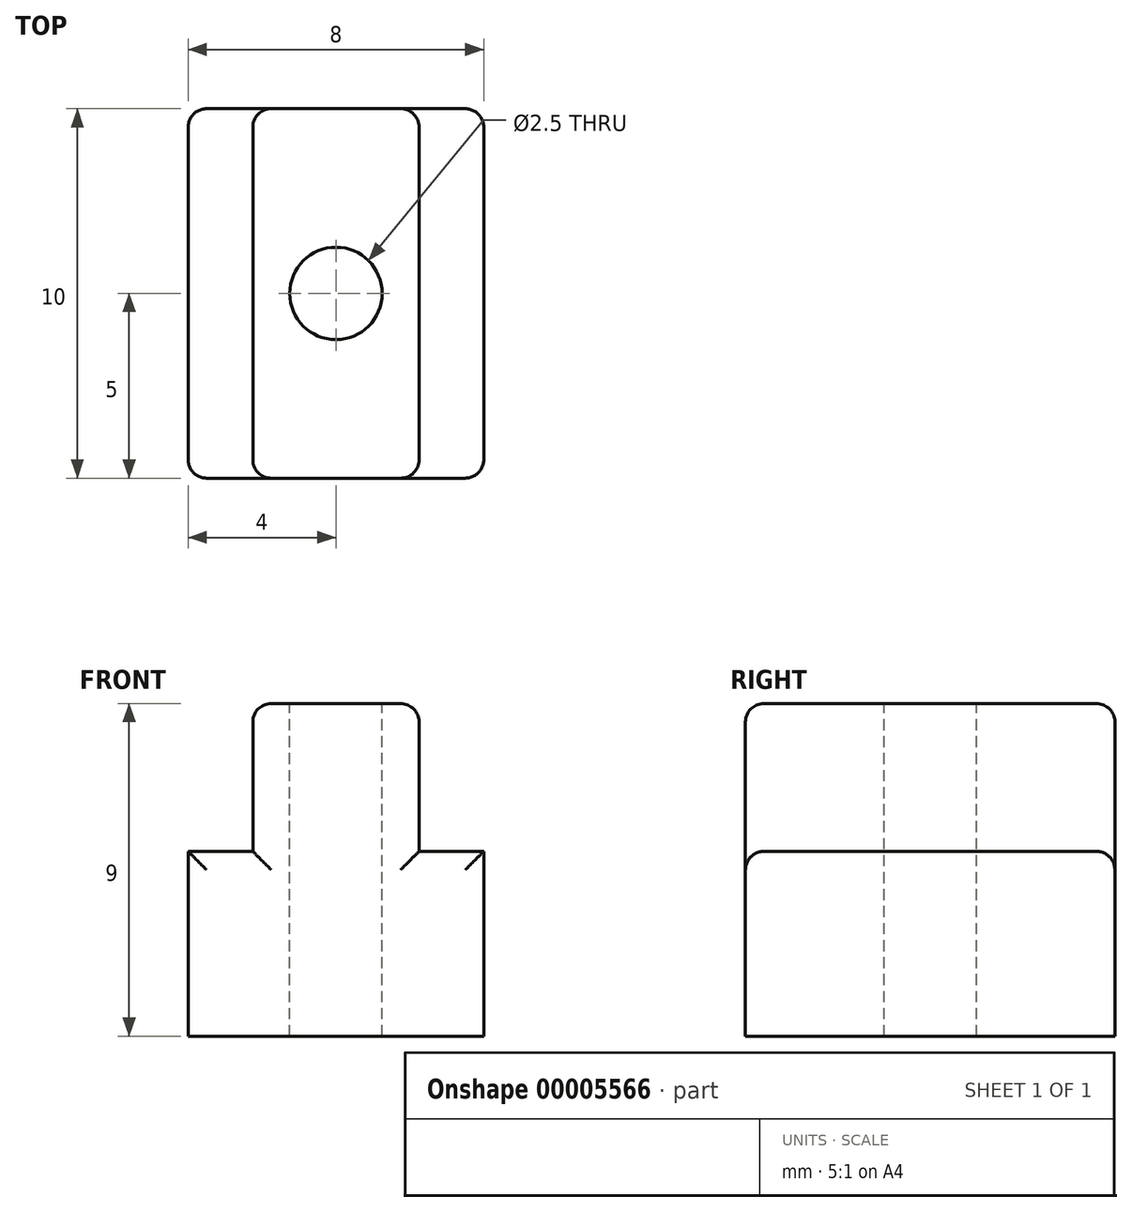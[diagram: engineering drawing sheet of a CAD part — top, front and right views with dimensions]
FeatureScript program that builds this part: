
annotation { "Feature Type Name" : "Feature", "Feature Type Description" : "" }
export const myFeature = defineFeature(function(context is Context, id is Id, definition is map)
    precondition{}
    {
        {
            var Q0;
            Q0=qCreatedBy(makeId("Front.planeOp"),FACE);
            var sketch = newSketch(context, id + "F0", { "sketchPlane" : qUnion([Q0])});
            skLineSegment(sketch, "E0.bottom", {"start": v(4, -5) * mm, "end": v(-4, -5) * mm});
            skLineSegment(sketch, "E0.top", {"start": v(4, 0) * mm, "end": v(-4, 0) * mm});
            skLineSegment(sketch, "E0.left", {"start": v(4, -5) * mm, "end": v(4, 0) * mm});
            skLineSegment(sketch, "E0.right", {"start": v(-4, -5) * mm, "end": v(-4, 0) * mm});
            skLineSegment(sketch, "E1.bottom", {"start": v(-2.25, 4) * mm, "end": v(2.25, 4) * mm});
            skLineSegment(sketch, "E1.top", {"start": v(-2.25, 0) * mm, "end": v(2.25, 0) * mm});
            skLineSegment(sketch, "E1.left", {"start": v(-2.25, 4) * mm, "end": v(-2.25, 0) * mm});
            skLineSegment(sketch, "E1.right", {"start": v(2.25, 4) * mm, "end": v(2.25, 0) * mm});
            skSolve(sketch);
        }
        {
            var Q0;
            {Q0=qUnion([makeQuery(id+"F0.imprint","IMPRINT",FACE,{"disambiguationData":[TD([[makeQuery(id+"F0.imprint","IMPRINT",EDGE,{"derivedFrom":sQuery(id+"F0.wireOp",EDGE,"E0.bottom")}),-1.0]])]}),makeQuery(id+"F0.imprint","IMPRINT",FACE,{"disambiguationData":[TD([[makeQuery(id+"F0.imprint","IMPRINT",EDGE,{"derivedFrom":sQuery(id+"F0.wireOp",EDGE,"E1.bottom")}),-1.0]])]})]);}
            extrude(context, id + "F1", {"entities" : qUnion([Q0]), "depth" : 10 * mm});
        }
        {
            var Q0;
            Q0=makeQuery(id+"F1.opExtrude","SWEPT_FACE",FACE,{"disambiguationData":[OSD([sQuery(id+"F0.wireOp",EDGE,"E1.bottom")])]});
            var sketch = newSketch(context, id + "F2", { "sketchPlane" : qUnion([Q0])});
            skLineSegment(sketch, "E2", {"start": v(0, -10) * mm, "end": v(0, 0) * mm, "construction": true});
            skCircle(sketch, "E3", {"center": v(0, -5) * mm, "radius": 1.25 * mm});
            skSolve(sketch);
        }
        {
            var Q0;
            Q0=makeQuery(id+"F2.imprint","IMPRINT",FACE,{"disambiguationData":[TD([[makeQuery(id+"F2.imprint","IMPRINT",EDGE,{"derivedFrom":sQuery(id+"F2.wireOp",EDGE,"E3")}),1.0]])]});
            var Q1;
            Q1=makeQuery(id+"F1.opExtrude","SWEPT_FACE",FACE,{"disambiguationData":[OSD([sQuery(id+"F0.wireOp",EDGE,"E0.bottom")])]});
            extrude(context, id + "F3", {"entities" : qUnion([Q0]), "operationType" : NewBodyOperationType.REMOVE, "endBound" : BoundingType.UP_TO_SURFACE, "oppositeDirection" : true, "endBoundEntityFace" : qUnion([Q1]), "depth" : 25 * mm});
        }
        {
            var Q0;
            Q0=makeQuery(id+"F1.opExtrude","SWEPT_EDGE",EDGE,{"disambiguationData":[OSD([sQuery(id+"F0.wireOp",EDGE,"E1.bottom"),sQuery(id+"F0.wireOp",EDGE,"E1.right")])]});
            var Q1;
            Q1=makeQuery(id+"F1.opExtrude","CAP_EDGE",EDGE,{"disambiguationData":[OSD([sQuery(id+"F0.wireOp",EDGE,"E1.bottom")])],"isStart":false});
            var Q2;
            Q2=makeQuery(id+"F1.opExtrude","SWEPT_EDGE",EDGE,{"disambiguationData":[OSD([sQuery(id+"F0.wireOp",EDGE,"E1.bottom"),sQuery(id+"F0.wireOp",EDGE,"E1.left")])]});
            var Q3;
            Q3=makeQuery(id+"F1.opExtrude","CAP_EDGE",EDGE,{"disambiguationData":[OSD([sQuery(id+"F0.wireOp",EDGE,"E1.bottom")])],"isStart":true});
            var Q4;
            Q4=makeQuery(id+"F1.opExtrude","CAP_EDGE",EDGE,{"disambiguationData":[OSD([sQuery(id+"F0.wireOp",EDGE,"E1.left")])],"isStart":true});
            var Q5;
            {var subQ0=sQuery(id+"F0.wireOp",EDGE,"E0.top");Q5=makeQuery(id+"F1.opExtrude","CAP_EDGE",EDGE,{"disambiguationData":[OSD([subQ0]),TDD([makeQuery(id+"F0.imprint","IMPRINT",EDGE,{"disambiguationData":[TD([[makeQuery(id+"F0.imprint","INTERSECT",VERTEX,{"derivedFrom":[subQ0,sQuery(id+"F0.wireOp",EDGE,"E0.right")]}),1.0]])],"derivedFrom":subQ0})])],"isStart":true});}
            var Q6;
            Q6=makeQuery(id+"F1.opExtrude","CAP_EDGE",EDGE,{"disambiguationData":[OSD([sQuery(id+"F0.wireOp",EDGE,"E0.right")])],"isStart":true});
            var Q7;
            {var subQ0=sQuery(id+"F0.wireOp",EDGE,"E0.top");Q7=makeQuery(id+"F1.opExtrude","CAP_EDGE",EDGE,{"disambiguationData":[OSD([subQ0]),TDD([makeQuery(id+"F0.imprint","IMPRINT",EDGE,{"disambiguationData":[TD([[makeQuery(id+"F0.imprint","INTERSECT",VERTEX,{"derivedFrom":[subQ0,sQuery(id+"F0.wireOp",EDGE,"E0.right")]}),1.0]])],"derivedFrom":subQ0})])],"isStart":false});}
            var Q8;
            Q8=makeQuery(id+"F1.opExtrude","CAP_EDGE",EDGE,{"disambiguationData":[OSD([sQuery(id+"F0.wireOp",EDGE,"E1.left")])],"isStart":false});
            var Q9;
            Q9=makeQuery(id+"F1.opExtrude","CAP_EDGE",EDGE,{"disambiguationData":[OSD([sQuery(id+"F0.wireOp",EDGE,"E0.right")])],"isStart":false});
            var Q10;
            Q10=makeQuery(id+"F1.opExtrude","CAP_EDGE",EDGE,{"disambiguationData":[OSD([sQuery(id+"F0.wireOp",EDGE,"E1.right")])],"isStart":true});
            var Q11;
            {var subQ0=sQuery(id+"F0.wireOp",EDGE,"E0.top");Q11=makeQuery(id+"F1.opExtrude","CAP_EDGE",EDGE,{"disambiguationData":[OSD([subQ0]),TDD([makeQuery(id+"F0.imprint","IMPRINT",EDGE,{"disambiguationData":[TD([[makeQuery(id+"F0.imprint","INTERSECT",VERTEX,{"derivedFrom":[subQ0,sQuery(id+"F0.wireOp",EDGE,"E0.left")]}),-1.0]])],"derivedFrom":subQ0})])],"isStart":true});}
            var Q12;
            Q12=makeQuery(id+"F1.opExtrude","CAP_EDGE",EDGE,{"disambiguationData":[OSD([sQuery(id+"F0.wireOp",EDGE,"E0.left")])],"isStart":true});
            var Q13;
            Q13=makeQuery(id+"F1.opExtrude","CAP_EDGE",EDGE,{"disambiguationData":[OSD([sQuery(id+"F0.wireOp",EDGE,"E0.left")])],"isStart":false});
            var Q14;
            {var subQ0=sQuery(id+"F0.wireOp",EDGE,"E0.top");Q14=makeQuery(id+"F1.opExtrude","CAP_EDGE",EDGE,{"disambiguationData":[OSD([subQ0]),TDD([makeQuery(id+"F0.imprint","IMPRINT",EDGE,{"disambiguationData":[TD([[makeQuery(id+"F0.imprint","INTERSECT",VERTEX,{"derivedFrom":[subQ0,sQuery(id+"F0.wireOp",EDGE,"E0.left")]}),-1.0]])],"derivedFrom":subQ0})])],"isStart":false});}
            var Q15;
            Q15=makeQuery(id+"F1.opExtrude","CAP_EDGE",EDGE,{"disambiguationData":[OSD([sQuery(id+"F0.wireOp",EDGE,"E1.right")])],"isStart":false});
            fillet(context, id + "F4", {"entities" : qUnion([Q0, Q1, Q2, Q3, Q4, Q5, Q6, Q7, Q8, Q9, Q10, Q11, Q12, Q13, Q14, Q15]), "radius" : 0.5 * mm, "tangentPropagation" : true, "allowEdgeOverflow" : false});
        }
    });
